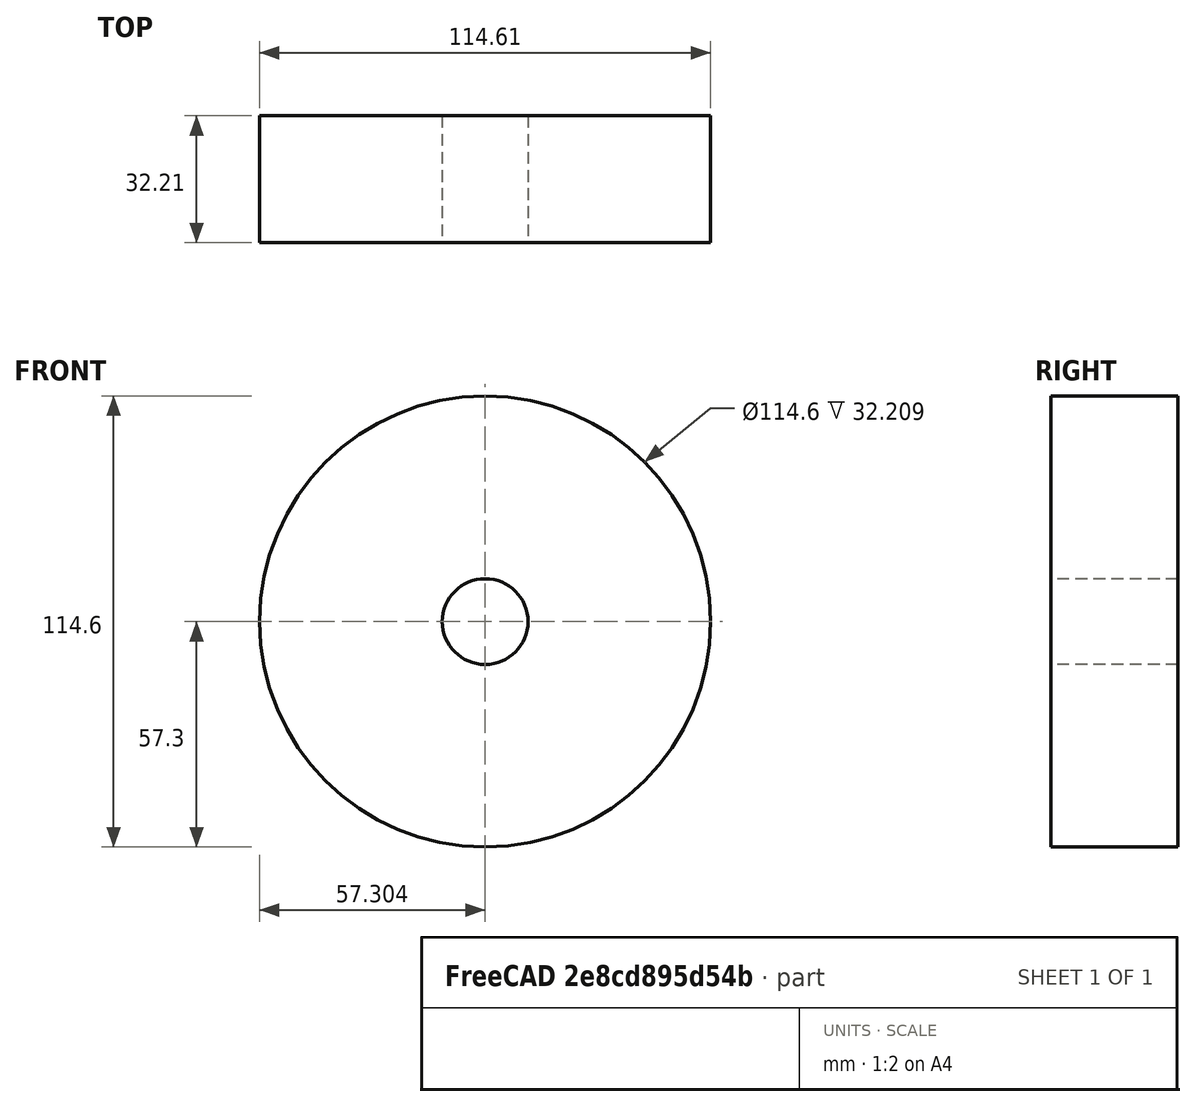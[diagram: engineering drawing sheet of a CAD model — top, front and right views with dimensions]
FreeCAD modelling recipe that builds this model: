
FCSTD DOCUMENT  (FreeCAD 0.20R29410 (Git))
Label: MangoJelly_Solutions_Tutorial_Ep8_5
License: All rights reserved
LicenseURL: http://en.wikipedia.org/wiki/All_rights_reserved
objects: Sketcher::SketchObject×1, Part::Revolution×1
note: 2 computed .brp shape members not serialized (recipe doc carries the construction recipe); baked Part::Feature solids carry a one-line shape summary decoded from their .brp

FEATURE [Sketcher::SketchObject] Sketch
  FullyConstrained = false
  sketch-geometry (5):
    g0: LineSegment StartX=-39.6581 StartY=36.2817 StartZ=0 EndX=6.75108 EndY=36.2817 EndZ=0
    g1: LineSegment StartX=6.75108 StartY=36.2817 StartZ=0 EndX=6.75108 EndY=4.07288 EndZ=0
    g2: LineSegment StartX=6.75108 StartY=4.07288 StartZ=0 EndX=-39.6581 EndY=4.07288 EndZ=0
    g3: LineSegment StartX=-39.6581 StartY=4.07288 StartZ=0 EndX=-39.6581 EndY=36.2817 EndZ=0
    g4: LineSegment StartX=17.6436 StartY=38.1647 StartZ=0 EndX=17.6436 EndY=1.12764 EndZ=0
  constraints (9):
    c: Coincident(g0,g1)
    c: Coincident(g1,g2)
    c: Coincident(g2,g3)
    c: Coincident(g3,g0)
    c: Horizontal(g0)
    c: Horizontal(g2)
    c: Vertical(g1)
    c: Vertical(g3)
    c: Vertical(g4)
FEATURE [Part::Revolution] Revolve
  Angle = 360
  Axis = (0,-1,0)
  AxisLink = -> Sketch [Edge5]
  Base = (17.6436,1.12764,0)
  FaceMakerClass = Part::FaceMakerBullseye
  Solid = false
  Source = -> Sketch
  Symmetric = false
